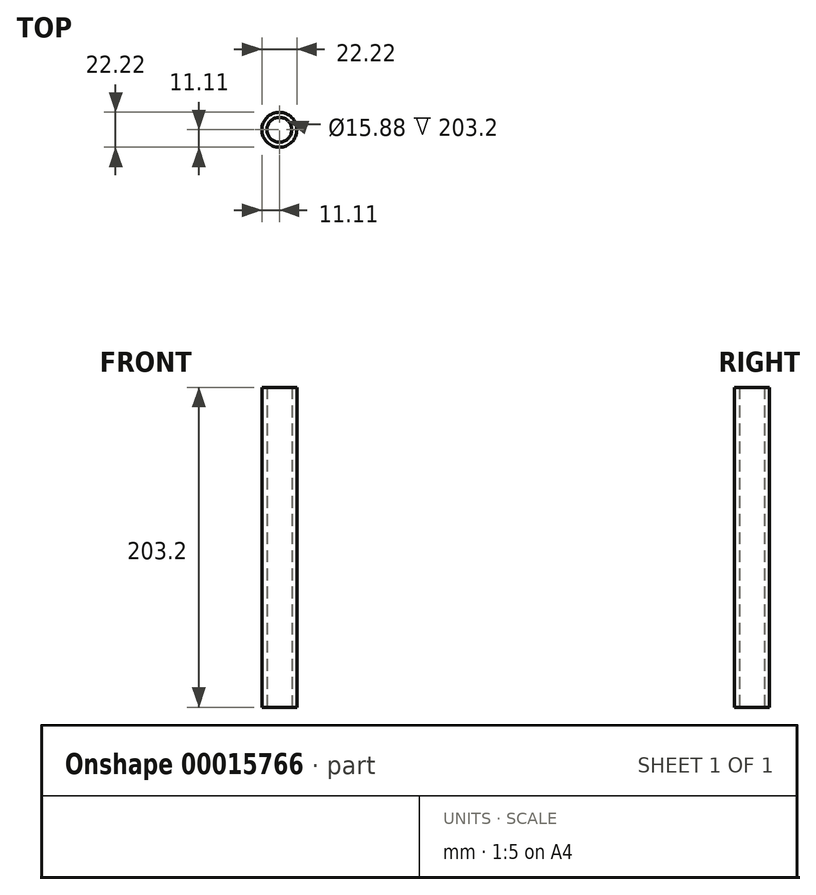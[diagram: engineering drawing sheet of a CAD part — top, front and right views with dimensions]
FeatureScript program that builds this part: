
annotation { "Feature Type Name" : "Feature", "Feature Type Description" : "" }
export const myFeature = defineFeature(function(context is Context, id is Id, definition is map)
    precondition{}
    {
        {
            var Q0;
            Q0=qCreatedBy(makeId("Top.planeOp"),FACE);
            var sketch = newSketch(context, id + "F0", { "sketchPlane" : qUnion([Q0])});
            skCircle(sketch, "E0", {"center": v(0, 0) * mm, "radius": 11.11 * mm});
            skCircle(sketch, "E1", {"center": v(0, 0) * mm, "radius": 7.94 * mm});
            skSolve(sketch);
        }
        {
            var Q0;
            Q0=qSketchRegion(id+"F0",true);
            extrude(context, id + "F1", {"entities" : qUnion([Q0]), "depth" : 203.2 * mm});
        }
    });
